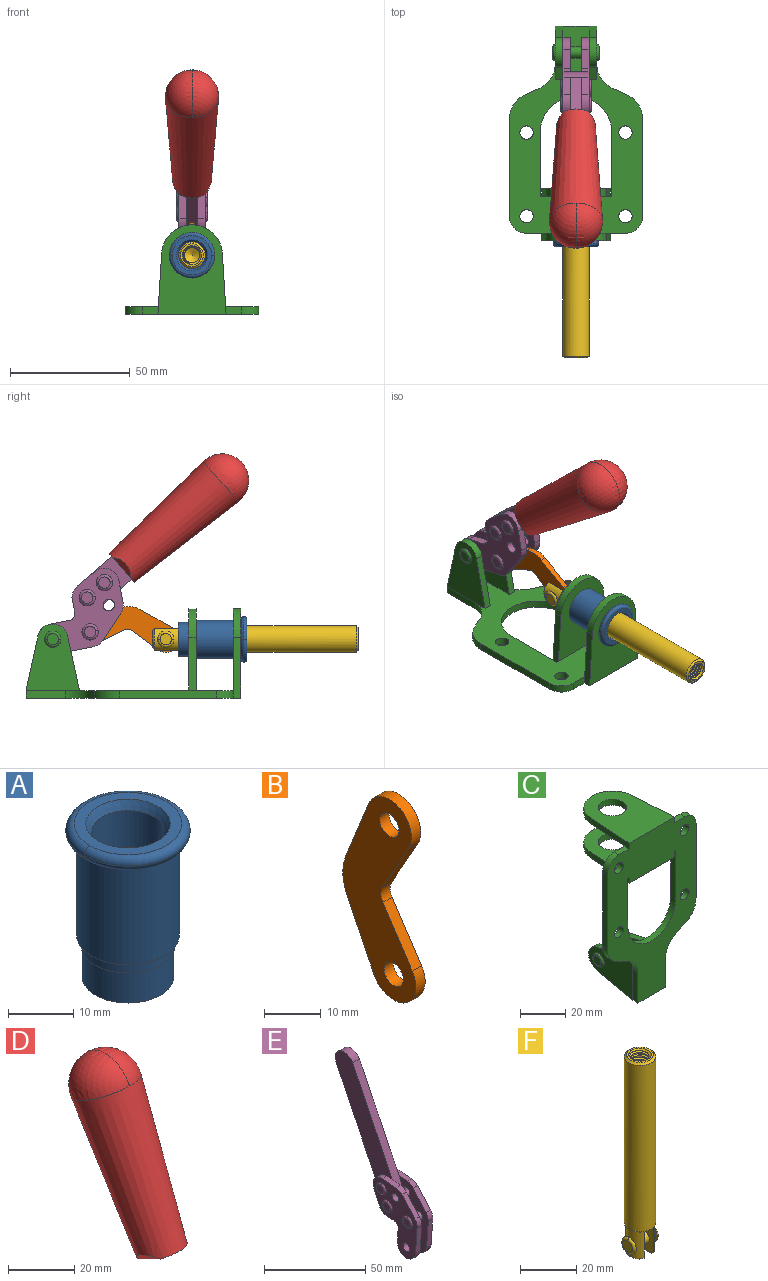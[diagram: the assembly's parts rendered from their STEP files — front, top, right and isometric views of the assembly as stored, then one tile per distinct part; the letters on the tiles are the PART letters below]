
ASSEMBLY  parts=6 mates=6
PART A: 15 faces, bbox 20.6x20.6x28.7 mm
  f0: torus R=8.26mm, axis (0,0,1), area 56.8mm2, adj f1,f10,f12
  f1: torus R=8.26mm, axis (0,0,1), area 56.8mm2, adj f0,f6,f13
  f2: cylinder r=5.59mm len=25.91mm, axis (0,0,1), area 909.6mm2, adj f3,f4
  f3: cone r=6.86mm half-angle=45deg, axis (0,0,-1), area 70.2mm2, adj f2,f14
  f4: cone r=6.47mm half-angle=30deg, axis (0,0,1), area 66.7mm2, adj f2,f13
  f5: cylinder r=7.04mm len=14.07mm, axis (0,0,1), area 252.6mm2, adj f11,f14
  f6: torus R=8.26mm, axis (0,0,1), area 56.8mm2, adj f1,f12,f13
  f7: cylinder r=7.16mm len=14.33mm, axis (0,0,1), area 91.5mm2, adj f9,f11
  f8: cylinder r=7.86mm len=18.42mm, axis (0,0,1), area 909.6mm2, adj f9,f10
  f9: plane 15.72x15.72mm, normal (0,0,-1), area 33mm2, adj f7,f8
  f10: plane 16.51x16.51mm, normal (0,0,-1), area 19.9mm2, adj f0,f8,f12
  f11: plane 14.33x14.33mm, normal (0,0,-1), area 5.7mm2, adj f5,f7
  f12: torus R=8.26mm, axis (0,0,1), area 56.8mm2, adj f0,f6,f10
  f13: plane 16.51x16.51mm, normal (0,0,1), area 82.7mm2, adj f1,f4,f6
  f14: plane 14.07x14.07mm, normal (0,0,-1), area 7.8mm2, adj f3,f5
PART B: 12 faces, bbox 2.3x18.2x42.8 mm
  f0: cylinder r=2.4mm len=4.8mm, axis (1,0,0), area 34.9mm2, adj f4,f11
  f1: cylinder r=10.41mm len=8.47mm, axis (1,0,0), area 20.2mm2, adj f4,f9,f10,f11
  f2: cylinder r=3.05mm len=3.16mm, axis (1,0,0), area 7.7mm2, adj f4,f6,f7,f11
  f3: cylinder r=2.4mm len=4.8mm, axis (1,0,0), area 34.9mm2, adj f4,f11
  f4: plane 42.81x18.23mm, normal (-1,0,0), area 414.1mm2, adj f0,f1,f2,f3,f5,f6,f7,f8
  f5: cylinder r=5.54mm len=10.67mm, axis (1,0,0), area 41.8mm2, adj f4,f6,f10,f11
  f6: plane 11.66x6.53mm, normal (0,-0.87,-0.49), area 30.9mm2, adj f2,f4,f5,f11
  f7: plane 11.17x7.33mm, normal (0,-0.84,0.55), area 30.9mm2, adj f2,f4,f8,f11
  f8: cylinder r=5.54mm len=10.51mm, axis (1,0,0), area 41.8mm2, adj f4,f7,f9,f11
  f9: plane 13.67x6.67mm, normal (0,0.9,-0.44), area 35.1mm2, adj f1,f4,f8,f11
  f10: plane 14.1x5.7mm, normal (0,0.93,0.37), area 35.1mm2, adj f1,f4,f5,f11
  f11: plane 42.81x18.23mm, normal (1,0,0), area 414.1mm2, adj f0,f1,f2,f3,f5,f6,f7,f8
PART C: 55 faces, bbox 55.7x37.4x89.8 mm
  f0: torus R=2.41mm, axis (-1,0,0), area 15mm2, adj f11,f15,f25
  f1: torus R=2.41mm, axis (-1,0,0), area 15mm2, adj f10,f12,f22
  f2: cylinder r=2.78mm len=5.56mm, axis (0,-1,0), area 54.2mm2, adj f30,f54
  f3: cylinder r=14.99mm len=29.97mm, axis (0,-1,0), area 145.9mm2, adj f30,f49,f53,f54
  f4: cylinder r=2.78mm len=5.56mm, axis (0,-1,0), area 54.2mm2, adj f30,f54
  f5: cylinder r=2.78mm len=5.56mm, axis (0,-1,0), area 54.2mm2, adj f30,f54
  f6: cylinder r=2.78mm len=5.56mm, axis (0,-1,0), area 54.2mm2, adj f30,f54
  f7: cylinder r=6.35mm len=12.7mm, axis (0,0,1), area 123.6mm2, adj f27,f51
  f8: cylinder r=6.35mm len=12.7mm, axis (0,0,-1), area 124.7mm2, adj f21,f35
  f9: cylinder r=2.41mm len=11.18mm, axis (-1,0,0), area 169.4mm2, adj f16,f19
  f10: plane 4.83x4.83mm, normal (1,0,0), area 18.3mm2, adj f1,f12
  f11: plane 4.83x4.83mm, normal (-1,0,0), area 18.3mm2, adj f0,f15
  f12: torus R=2.41mm, axis (-1,0,0), area 15mm2, adj f1,f10,f22
  f13: cylinder r=6.35mm len=12.41mm, axis (1,0,0), area 53.4mm2, adj f18,f19,f22,f23
  f14: cylinder r=6.35mm len=12.41mm, axis (-1,0,0), area 53.4mm2, adj f16,f17,f24,f25
  f15: torus R=2.41mm, axis (-1,0,0), area 15mm2, adj f0,f11,f25
  f16: plane 27.86x22.35mm, normal (1,0,0), area 425.4mm2, adj f9,f14,f17,f24,f30
  f17: plane 22.86x4.97mm, normal (0,0.21,0.98), area 72.5mm2, adj f14,f16,f25,f30
  f18: plane 22.86x4.97mm, normal (0,0.21,0.98), area 72.5mm2, adj f13,f19,f22,f30
  f19: plane 27.86x22.35mm, normal (-1,0,0), area 425.4mm2, adj f9,f13,f18,f23,f30
  f20: cylinder r=12.7mm len=25.35mm, axis (0,0,-1), area 119.8mm2, adj f21,f34,f35,f36
  f21: plane 34.21x28.07mm, normal (0,0,-1), area 702.4mm2, adj f8,f20,f30,f34,f36
  f22: plane 27.96x22.45mm, normal (1,0,0), area 407.2mm2, adj f1,f12,f13,f18,f23,f30,f42,f43
  f23: plane 22.86x4.97mm, normal (0,0.21,-0.98), area 72.5mm2, adj f13,f19,f22,f44
  f24: plane 22.86x4.97mm, normal (0,0.21,-0.98), area 72.5mm2, adj f14,f16,f25,f44
  f25: plane 27.86x22.35mm, normal (-1,0,0), area 407.1mm2, adj f0,f14,f15,f17,f24,f30,f45,f46
  f26: plane 3.1x0.95mm, normal (0,0,-1), area 2.7mm2, adj f30,f49,f50,f54
  f27: plane 34.21x28.07mm, normal (0,0,1), area 702.4mm2, adj f7,f28,f30,f50,f52
  f28: cylinder r=12.7mm len=25.35mm, axis (0,0,1), area 118.8mm2, adj f27,f50,f51,f52
  f29: plane 3.1x0.95mm, normal (0,0,-1), area 2.7mm2, adj f30,f52,f53,f54
  f30: plane 86.54x55.63mm, normal (0,1,0), area 2362.9mm2, adj f2,f3,f4,f5,f6,f16,f17,f18
  f31: plane 40.56x3.1mm, normal (-1,0,0), area 125.7mm2, adj f30,f32,f48,f54
  f32: cylinder r=7.11mm len=7.11mm, axis (0,-1,0), area 34.6mm2, adj f30,f31,f33,f54
  f33: plane 6.67x3.1mm, normal (0,0,1), area 20.4mm2, adj f30,f32,f34,f54
  f34: plane 25.39x3.13mm, normal (-1,0.06,0), area 79.5mm2, adj f20,f21,f33,f35,f54
  f35: plane 37.31x28.45mm, normal (0,0,1), area 789.9mm2, adj f8,f20,f34,f36,f54
  f36: plane 25.39x3.13mm, normal (1,0.06,0), area 79.5mm2, adj f20,f21,f35,f37,f54
  f37: plane 6.67x3.1mm, normal (0,0,1), area 20.4mm2, adj f30,f36,f38,f54
  f38: cylinder r=7.11mm len=7.11mm, axis (0,-1,0), area 34.6mm2, adj f30,f37,f39,f54
  f39: plane 40.56x3.1mm, normal (1,0,0), area 125.7mm2, adj f30,f38,f40,f54
  f40: cylinder r=11.18mm len=10.16mm, axis (0,-1,0), area 39.5mm2, adj f30,f39,f41,f54
  f41: plane 6.09x3.1mm, normal (0.42,0,-0.91), area 20.8mm2, adj f30,f40,f42,f54
  f42: cylinder r=11.18mm len=9.41mm, axis (0,-1,0), area 37.2mm2, adj f22,f30,f41,f43,f54
  f43: plane 16.5x3.1mm, normal (1,0,0), area 51.1mm2, adj f22,f42,f44,f54
  f44: plane 17.37x3.1mm, normal (0,0,-1), area 53.8mm2, adj f23,f24,f30,f43,f45,f54
  f45: plane 16.5x3.1mm, normal (-1,0,0), area 51.1mm2, adj f25,f44,f46,f54
  f46: cylinder r=11.18mm len=9.41mm, axis (0,-1,0), area 37.2mm2, adj f25,f30,f45,f47,f54
  f47: plane 6.09x3.1mm, normal (-0.42,0,-0.91), area 20.8mm2, adj f30,f46,f48,f54
  f48: cylinder r=11.18mm len=10.16mm, axis (0,-1,0), area 39.5mm2, adj f30,f31,f47,f54
  f49: plane 26.54x3.1mm, normal (-1,0,0), area 82.3mm2, adj f3,f26,f30,f54
  f50: plane 25.39x3.1mm, normal (1,0.06,0), area 78.8mm2, adj f26,f27,f28,f51,f54
  f51: plane 37.31x28.45mm, normal (0,0,-1), area 789.9mm2, adj f7,f28,f50,f52,f54
  f52: plane 25.39x3.1mm, normal (-1,0.06,0), area 78.8mm2, adj f27,f28,f29,f51,f54
  f53: plane 26.54x3.1mm, normal (1,0,0), area 82.3mm2, adj f3,f29,f30,f54
  f54: plane 89.66x55.63mm, normal (0,-1,0), area 2678.5mm2, adj f2,f3,f4,f5,f6,f26,f29,f31
PART D: 11 faces, bbox 22.3x42.6x64.5 mm
  f0: sphere r=11.13mm, area 411.4mm2, adj f1,f8
  f1: cone r=11.11mm half-angle=3.3deg, axis (0,0.44,0.9), area 3251.8mm2, adj f0,f7,f8,f9,f10
  f2: cylinder r=6.16mm len=11.7mm, axis (1,0,0), area 89.5mm2, adj f3,f4,f5,f6
  f3: plane 60.23x36.75mm, normal (-1,0,0), area 763.6mm2, adj f2,f4,f6,f10
  f4: plane 51.37x25.05mm, normal (0,0.9,-0.44), area 264.2mm2, adj f2,f3,f5,f10
  f5: plane 60.23x36.75mm, normal (1,0,0), area 763.6mm2, adj f2,f4,f6,f10
  f6: plane 51.37x25.05mm, normal (0,-0.9,0.44), area 264.2mm2, adj f2,f3,f5,f10
  f7: plane 9.95x5.95mm, normal (0.71,-0.31,-0.64), area 25.8mm2, adj f1,f10
  f8: sphere r=11.13mm, area 411.4mm2, adj f0,f1
  f9: plane 9.95x5.95mm, normal (-0.71,-0.31,-0.64), area 25.8mm2, adj f1,f10
  f10: plane 14.27x11.38mm, normal (0,-0.44,-0.9), area 106.7mm2, adj f1,f3,f4,f5,f6,f7,f9
PART E: 59 faces, bbox 12.9x60.2x99.6 mm
  f0: torus R=2.39mm, axis (-1,0,0), area 14.9mm2, adj f20,f43,f51
  f1: torus R=2.39mm, axis (-1,0,0), area 14.9mm2, adj f19,f42,f51
  f2: torus R=2.39mm, axis (-1,0,0), area 14.9mm2, adj f18,f35,f51
  f3: torus R=2.39mm, axis (-1,0,0), area 14.9mm2, adj f14,f17,f23
  f4: torus R=2.39mm, axis (-1,0,0), area 14.9mm2, adj f13,f16,f23
  f5: torus R=2.39mm, axis (-1,0,0), area 14.9mm2, adj f12,f15,f23
  f6: cylinder r=2.39mm len=4.78mm, axis (1,0,0), area 46.5mm2, adj f48,f50,f51
  f7: cylinder r=2.39mm len=4.78mm, axis (1,0,0), area 46.5mm2, adj f50,f51
  f8: cylinder r=6.35mm len=12.68mm, axis (1,0,0), area 61.8mm2, adj f38,f39,f50,f51
  f9: cylinder r=2.39mm len=4.78mm, axis (-1,0,0), area 70.5mm2, adj f46,f50
  f10: cylinder r=2.39mm len=4.78mm, axis (-1,0,0), area 46.5mm2, adj f23,f45,f46
  f11: cylinder r=2.39mm len=4.78mm, axis (-1,0,0), area 46.5mm2, adj f23,f46
  f12: plane 4.78x4.78mm, normal (1,0,0), area 17.9mm2, adj f5,f15
  f13: plane 4.78x4.78mm, normal (1,0,0), area 17.9mm2, adj f4,f16
  f14: plane 4.78x4.78mm, normal (1,0,0), area 17.9mm2, adj f3,f17
  f15: torus R=2.39mm, axis (-1,0,0), area 14.9mm2, adj f5,f12,f23
  f16: torus R=2.39mm, axis (-1,0,0), area 14.9mm2, adj f4,f13,f23
  f17: torus R=2.39mm, axis (-1,0,0), area 14.9mm2, adj f3,f14,f23
  f18: plane 4.78x4.78mm, normal (-1,0,0), area 17.9mm2, adj f2,f35
  f19: plane 4.78x4.78mm, normal (-1,0,0), area 17.9mm2, adj f1,f42
  f20: plane 4.78x4.78mm, normal (-1,0,0), area 17.9mm2, adj f0,f43
  f21: plane 2.26x0.2mm, normal (1,0,0), area 0.2mm2, adj f31,f44
  f22: plane 2.26x0.2mm, normal (-1,0,0), area 0.2mm2, adj f41,f44
  f23: plane 39.37x30.77mm, normal (1,0,0), area 565.5mm2, adj f3,f4,f5,f10,f11,f15,f16,f17
  f24: cylinder r=6.1mm len=4.15mm, axis (-1,0,0), area 14.7mm2, adj f23,f25,f32,f46
  f25: plane 10.25x9.01mm, normal (0,-0.75,0.66), area 42.3mm2, adj f23,f24,f26,f46
  f26: cylinder r=6.35mm len=4.64mm, axis (-1,0,0), area 15.6mm2, adj f23,f25,f27,f46
  f27: plane 15.84x3.1mm, normal (0,-1,-0.07), area 49.2mm2, adj f23,f26,f28,f46
  f28: cylinder r=6.35mm len=12.68mm, axis (-1,0,0), area 61.8mm2, adj f23,f27,f29,f46
  f29: plane 8.11x3.1mm, normal (0,1,0.07), area 25.2mm2, adj f23,f28,f30,f46
  f30: cylinder r=3.05mm len=3.25mm, axis (-1,0,0), area 14.8mm2, adj f23,f29,f31,f46
  f31: plane 5.99x3.1mm, normal (0,0.07,-1), area 18.6mm2, adj f21,f23,f30,f44,f46
  f32: plane 9.5x3.1mm, normal (0,-0.07,1), area 29.5mm2, adj f23,f24,f33,f46,f47
  f33: cylinder r=6.1mm len=8.63mm, axis (-1,0,0), area 39.1mm2, adj f23,f32,f34,f47
  f34: plane 8.65x3.96mm, normal (0,0.91,-0.42), area 29.5mm2, adj f23,f33,f44,f47
  f35: torus R=2.39mm, axis (-1,0,0), area 14.9mm2, adj f2,f18,f51
  f36: plane 10.25x9.01mm, normal (0,-0.75,0.66), area 42.3mm2, adj f37,f49,f50,f51
  f37: cylinder r=6.35mm len=4.64mm, axis (1,0,0), area 15.6mm2, adj f36,f38,f50,f51
  f38: plane 15.84x3.1mm, normal (0,-1,-0.07), area 49.2mm2, adj f8,f37,f50,f51
  f39: plane 8.11x3.1mm, normal (0,1,0.07), area 25.2mm2, adj f8,f40,f50,f51
  f40: cylinder r=3.05mm len=3.25mm, axis (1,0,0), area 14.8mm2, adj f39,f41,f50,f51
  f41: plane 5.99x3.1mm, normal (0,0.07,-1), area 18.6mm2, adj f22,f40,f44,f50,f51
  f42: torus R=2.39mm, axis (-1,0,0), area 14.9mm2, adj f1,f19,f51
  f43: torus R=2.39mm, axis (-1,0,0), area 14.9mm2, adj f0,f20,f51
  f44: cylinder r=6.35mm len=12.12mm, axis (-1,0,0), area 128.9mm2, adj f21,f22,f23,f31,f34,f41,f46,f47
  f45: plane 2.65x1.35mm, normal (1,0,0), area 1mm2, adj f10,f55
  f46: plane 39.08x20.42mm, normal (-1,0,0), area 412.5mm2, adj f9,f10,f11,f24,f25,f26,f27,f28
  f47: plane 77.62x39.82mm, normal (1,0,0), area 850mm2, adj f32,f33,f34,f44,f53,f54,f55
  f48: plane 2.65x1.35mm, normal (-1,0,0), area 1mm2, adj f6,f55
  f49: cylinder r=6.1mm len=4.15mm, axis (1,0,0), area 14.7mm2, adj f36,f50,f51,f56
  f50: plane 39.08x20.42mm, normal (1,0,0), area 412.5mm2, adj f6,f7,f8,f9,f36,f37,f38,f39
  f51: plane 39.37x30.77mm, normal (-1,0,0), area 565.5mm2, adj f0,f1,f2,f6,f7,f8,f35,f36
  f52: plane 8.65x3.96mm, normal (0,0.91,-0.42), area 29.5mm2, adj f44,f51,f57,f58
  f53: plane 68.49x33.4mm, normal (0,0.9,-0.44), area 358.1mm2, adj f44,f47,f54,f58
  f54: cylinder r=6.35mm len=12.06mm, axis (1,0,0), area 93.7mm2, adj f47,f53,f55,f58
  f55: plane 68.49x33.4mm, normal (0,-0.9,0.44), area 358.1mm2, adj f44,f45,f46,f47,f48,f50,f54,f58
  f56: plane 9.5x3.1mm, normal (0,-0.07,1), area 29.5mm2, adj f49,f50,f51,f57,f58
  f57: cylinder r=6.1mm len=8.63mm, axis (1,0,0), area 39.1mm2, adj f51,f52,f56,f58
  f58: plane 77.62x39.82mm, normal (-1,0,0), area 850mm2, adj f44,f52,f53,f54,f55,f56,f57
PART F: 48 faces, bbox 12.6x11.1x86.1 mm
  f0: torus R=2.41mm, axis (-1,0,0), area 15mm2, adj f30,f32,f34
  f1: torus R=2.41mm, axis (-1,0,0), area 15mm2, adj f29,f31,f33
  f2: cylinder r=5.54mm len=72.39mm, axis (0,0,1), area 2518.5mm2, adj f3,f4,f42,f43
  f3: cone r=5.54mm half-angle=45deg, axis (0,0,1), area 7.6mm2, adj f2,f5,f41
  f4: cone r=5.54mm half-angle=45deg, axis (0,0,-1), area 34.9mm2, adj f2,f39
  f5: cylinder r=5.08mm len=11.48mm, axis (0,0,1), area 108.3mm2, adj f3,f7,f8,f41
  f6: cylinder r=2.41mm len=4.83mm, axis (-1,0,0), area 71.2mm2, adj f40,f41
  f7: cylinder r=2.41mm len=4.83mm, axis (-1,0,0), area 7.6mm2, adj f5,f34
  f8: cone r=5.08mm half-angle=45deg, axis (0,0,1), area 10.6mm2, adj f5,f37,f41
  f9: cone r=3.98mm half-angle=45deg, axis (0,0,1), area 17.6mm2, adj f27,f39,f45,f46,f47
  f10: cylinder r=2.41mm len=4.83mm, axis (-1,0,0), area 7.6mm2, adj f33,f38
  f11: cylinder r=3.2mm len=6.4mm, axis (0,0,1), area 78.4mm2, adj f12,f28,f44,f45,f47
  f12: cylinder r=3.2mm len=6.4mm, axis (0,0,1), area 10.5mm2, adj f11,f13,f45,f47
  f13: cylinder r=3.2mm len=6.4mm, axis (0,0,1), area 10.5mm2, adj f12,f14,f45,f47
  f14: cylinder r=3.2mm len=6.4mm, axis (0,0,1), area 10.5mm2, adj f13,f15,f45,f47
  f15: cylinder r=3.2mm len=6.4mm, axis (0,0,1), area 10.5mm2, adj f14,f16,f45,f47
  f16: cylinder r=3.2mm len=6.4mm, axis (0,0,1), area 10.5mm2, adj f15,f17,f45,f47
  f17: cylinder r=3.2mm len=6.4mm, axis (0,0,1), area 10.5mm2, adj f16,f18,f45,f47
  f18: cylinder r=3.2mm len=6.4mm, axis (0,0,1), area 10.5mm2, adj f17,f19,f45,f47
  f19: cylinder r=3.2mm len=6.4mm, axis (0,0,1), area 10.5mm2, adj f18,f20,f45,f47
  f20: cylinder r=3.2mm len=6.4mm, axis (0,0,1), area 10.5mm2, adj f19,f21,f45,f47
  f21: cylinder r=3.2mm len=6.4mm, axis (0,0,1), area 10.5mm2, adj f20,f22,f45,f47
  f22: cylinder r=3.2mm len=6.4mm, axis (0,0,1), area 10.5mm2, adj f21,f23,f45,f47
  f23: cylinder r=3.2mm len=6.4mm, axis (0,0,1), area 10.5mm2, adj f22,f24,f45,f47
  f24: cylinder r=3.2mm len=6.4mm, axis (0,0,1), area 10.5mm2, adj f23,f25,f45,f47
  f25: cylinder r=3.2mm len=6.4mm, axis (0,0,1), area 10.5mm2, adj f24,f26,f45,f47
  f26: cylinder r=3.2mm len=6.4mm, axis (0,0,1), area 10.5mm2, adj f25,f27,f45,f47
  f27: cylinder r=3.2mm len=6.4mm, axis (0,0,1), area 7.4mm2, adj f9,f26,f45,f47
  f28: cone r=3.2mm half-angle=60deg, axis (0,0,1), area 37.2mm2, adj f11
  f29: plane 4.83x4.83mm, normal (-1,0,0), area 18.3mm2, adj f1,f31
  f30: plane 4.83x4.83mm, normal (1,0,0), area 18.3mm2, adj f0,f32
  f31: torus R=2.41mm, axis (-1,0,0), area 15mm2, adj f1,f29,f33
  f32: torus R=2.41mm, axis (-1,0,0), area 15mm2, adj f0,f30,f34
  f33: plane 6.83x6.83mm, normal (1,0,0), area 18.3mm2, adj f1,f10,f31
  f34: plane 6.83x6.83mm, normal (-1,0,0), area 18.3mm2, adj f0,f7,f32
  f35: cone r=5.08mm half-angle=45deg, axis (0,0,1), area 10.6mm2, adj f36,f38,f40
  f36: plane 7.25x1.97mm, normal (0,0,-1), area 10mm2, adj f35,f40
  f37: plane 7.25x1.97mm, normal (0,0,-1), area 10mm2, adj f8,f41
  f38: cylinder r=5.08mm len=11.48mm, axis (0,0,1), area 108.3mm2, adj f10,f35,f40,f42
  f39: plane 9.55x9.55mm, normal (0,0,1), area 22mm2, adj f4,f9
  f40: plane 12.76x10.09mm, normal (1,0,0), area 95.7mm2, adj f6,f35,f36,f38,f42,f43
  f41: plane 12.76x10.09mm, normal (-1,0,0), area 95.7mm2, adj f3,f5,f6,f8,f37,f43
  f42: cone r=5.54mm half-angle=45deg, axis (0,0,1), area 7.6mm2, adj f2,f38,f40
  f43: plane 11.07x4.7mm, normal (0,0,-1), area 50.4mm2, adj f2,f40,f41
  f44: plane 0.89x0.62mm, normal (-1,0,0), area 0.3mm2, adj f11,f45,f46,f47
  f45: bspline ~24.8x7.63mm, area 266.6mm2, adj f9,f11,f12,f13,f14,f15,f16,f17
  f46: bspline ~24.87x7.63mm, area 73.6mm2, adj f9,f44,f45,f47
  f47: bspline ~24.98x7.63mm, area 272.5mm2, adj f9,f11,f12,f13,f14,f15,f16,f17
PLACE A rot(axis=(1,0,0),90deg) t=(0,9.43,0)mm
PLACE B rot(axis=(1,0,0),97.5deg) t=(0,12.88,2.22)mm
PLACE C rot(axis=(1,0,0),90deg) t=(0,9.43,0)mm fixed
PLACE D rot(axis=(1,0,0),75deg) t=(0,4.15,9.14)mm
PLACE E rot(axis=(1,0,0),75deg) t=(0,4.15,9.14)mm
PLACE F rot(axis=(1,0,0),90deg) t=(0,9.81,0)mm
MATE revolute B.f3 <-> E.f4  axis (1,0,0) through (0,25.94,27.64)mm
MATE revolute B.f5 <-> F.f6  axis (1,0,0) through (0,-5.67,24.61)mm
MATE revolute E.f7 <-> C.f0  axis (1,0,0) through (0,41.52,24.61)mm
MATE slider A.f2 <-> F.f2  axis (0,1,0) through (0,-37.98,24.61)mm
MATE fastened D.f2 <-> E.f54  axis (1,0,0) through (0,-30.37,91.94)mm
MATE fastened C.f7 <-> A.f2  axis (0,-1,0) through (0,-36.96,24.61)mm
